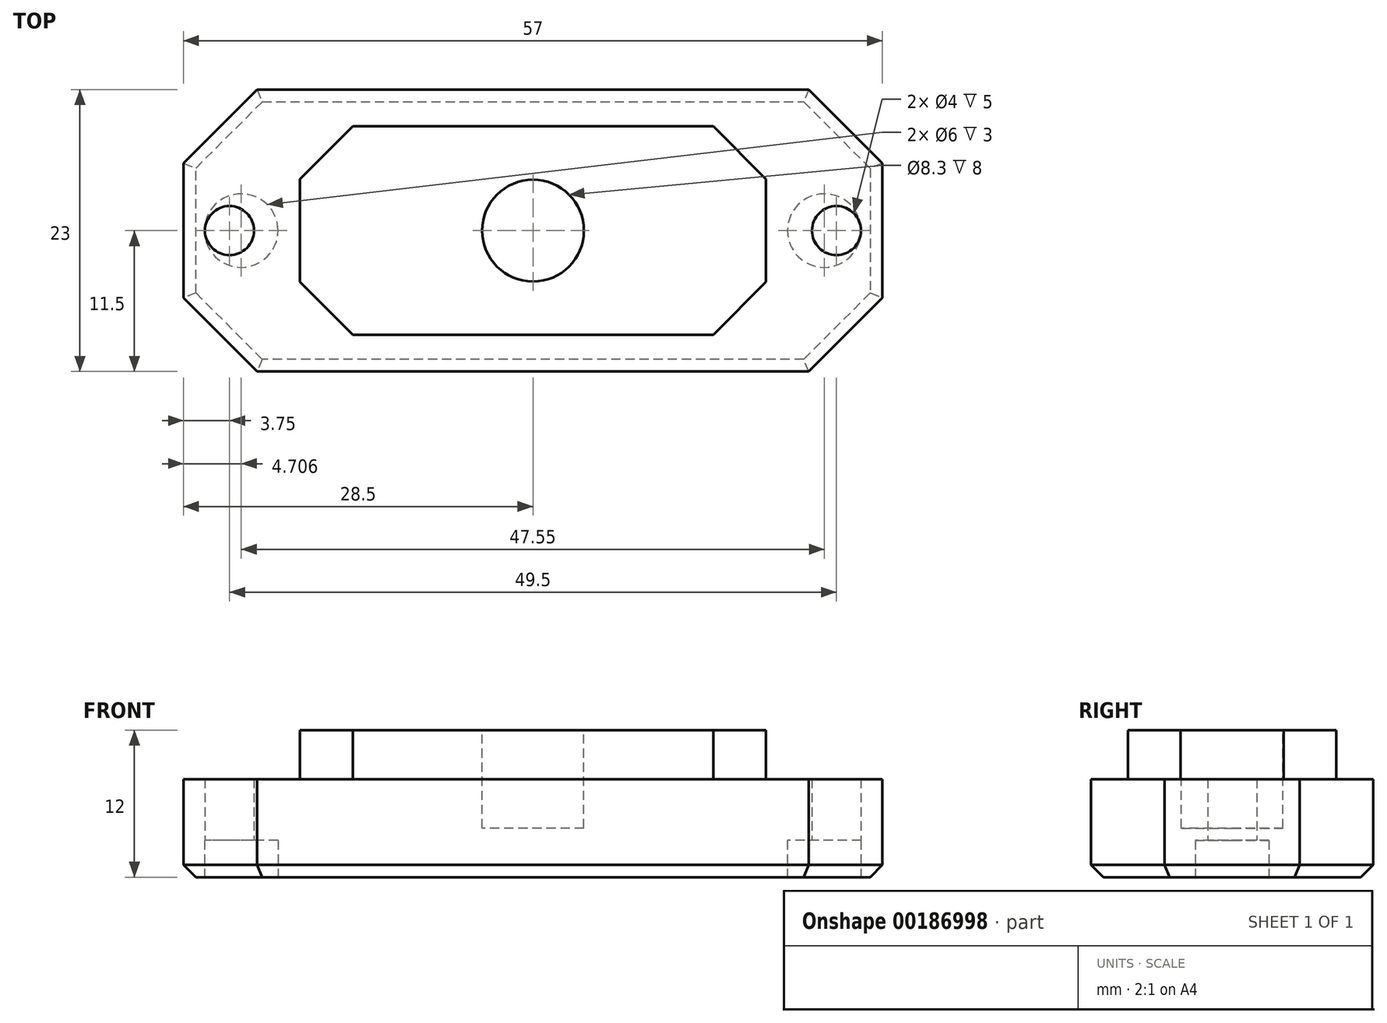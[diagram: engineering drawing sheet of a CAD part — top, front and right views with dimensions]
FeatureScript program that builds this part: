
annotation { "Feature Type Name" : "Feature", "Feature Type Description" : "" }
export const myFeature = defineFeature(function(context is Context, id is Id, definition is map)
    precondition{}
    {
        {
            var Q0;
            Q0=qCreatedBy(makeId("Top.planeOp"),FACE);
            var sketch = newSketch(context, id + "F0", { "sketchPlane" : qUnion([Q0])});
            skLineSegment(sketch, "E0.bottom", {"start": v(-14.7, 8.5) * mm, "end": v(14.7, 8.5) * mm});
            skLineSegment(sketch, "E0.top", {"start": v(-14.7, -8.5) * mm, "end": v(14.7, -8.5) * mm});
            skLineSegment(sketch, "E0.left", {"start": v(-19, 4.2) * mm, "end": v(-19, -4.2) * mm});
            skLineSegment(sketch, "E0.right", {"start": v(19, 4.2) * mm, "end": v(19, -4.2) * mm});
            skLineSegment(sketch, "E1.bottom", {"start": v(-22.5, 11.5) * mm, "end": v(22.5, 11.5) * mm});
            skLineSegment(sketch, "E1.top", {"start": v(-22.5, -11.5) * mm, "end": v(22.5, -11.5) * mm});
            skLineSegment(sketch, "E1.left", {"start": v(-28.5, 5.5) * mm, "end": v(-28.5, -5.5) * mm});
            skLineSegment(sketch, "E1.right", {"start": v(28.5, 5.5) * mm, "end": v(28.5, -5.5) * mm});
            skCircle(sketch, "E2", {"center": v(-24.75, 0) * mm, "radius": 2 * mm});
            skCircle(sketch, "E3.MirrorC", {"center": v(24.75, 0) * mm, "radius": 2 * mm});
            skLineSegment(sketch, "E4", {"start": v(-14.7, 8.5) * mm, "end": v(-19, 4.2) * mm});
            skLineSegment(sketch, "E5.MirrorCS", {"start": v(14.7, 8.5) * mm, "end": v(19, 4.2) * mm});
            skLineSegment(sketch, "E6.MirrorCS", {"start": v(-14.7, -8.5) * mm, "end": v(-19, -4.2) * mm});
            skLineSegment(sketch, "E7.MirrorCS", {"start": v(14.7, -8.5) * mm, "end": v(19, -4.2) * mm});
            skLineSegment(sketch, "E8", {"start": v(-28.5, 5.5) * mm, "end": v(-22.5, 11.5) * mm});
            skLineSegment(sketch, "E9.MirrorCS", {"start": v(28.5, 5.5) * mm, "end": v(22.5, 11.5) * mm});
            skLineSegment(sketch, "E10.MirrorCS", {"start": v(-28.5, -5.5) * mm, "end": v(-22.5, -11.5) * mm});
            skLineSegment(sketch, "E11.MirrorCS", {"start": v(28.5, -5.5) * mm, "end": v(22.5, -11.5) * mm});
            skPoint(sketch, "E12.orphan", {"position": v(-28.5, 11.5) * mm});
            skPoint(sketch, "E13.orphan", {"position": v(-19, 8.5) * mm});
            skSolve(sketch);
        }
        {
            var Q0;
            Q0=makeQuery(id+"F0.imprint","IMPRINT",FACE,{"disambiguationData":[TD([[makeQuery(id+"F0.imprint","IMPRINT",EDGE,{"derivedFrom":sQuery(id+"F0.wireOp",EDGE,"E0.bottom")}),-1.0]])]});
            extrude(context, id + "F1", {"entities" : qUnion([Q0]), "depth" : 12 * mm});
        }
        {
            var Q0;
            Q0=makeQuery(id+"F0.imprint","IMPRINT",FACE,{"disambiguationData":[TD([[makeQuery(id+"F0.imprint","IMPRINT",EDGE,{"derivedFrom":sQuery(id+"F0.wireOp",EDGE,"E0.bottom")}),1.0]])]});
            extrude(context, id + "F2", {"entities" : qUnion([Q0]), "operationType" : NewBodyOperationType.ADD, "depth" : 8 * mm});
        }
        {
            var Q0;
            Q0=makeQuery(id+"F2.opExtrude","CAP_EDGE",EDGE,{"disambiguationData":[OSD([sQuery(id+"F0.wireOp",EDGE,"E1.top")])],"isStart":true});
            var Q1;
            Q1=makeQuery(id+"F2.opExtrude","CAP_EDGE",EDGE,{"disambiguationData":[OSD([sQuery(id+"F0.wireOp",EDGE,"E10.MirrorCS")])],"isStart":true});
            var Q2;
            Q2=makeQuery(id+"F2.opExtrude","CAP_EDGE",EDGE,{"disambiguationData":[OSD([sQuery(id+"F0.wireOp",EDGE,"E1.left")])],"isStart":true});
            var Q3;
            Q3=makeQuery(id+"F2.opExtrude","CAP_EDGE",EDGE,{"disambiguationData":[OSD([sQuery(id+"F0.wireOp",EDGE,"E8")])],"isStart":true});
            var Q4;
            Q4=makeQuery(id+"F2.opExtrude","CAP_EDGE",EDGE,{"disambiguationData":[OSD([sQuery(id+"F0.wireOp",EDGE,"E1.bottom")])],"isStart":true});
            var Q5;
            Q5=makeQuery(id+"F2.opExtrude","CAP_EDGE",EDGE,{"disambiguationData":[OSD([sQuery(id+"F0.wireOp",EDGE,"E9.MirrorCS")])],"isStart":true});
            var Q6;
            Q6=makeQuery(id+"F2.opExtrude","CAP_EDGE",EDGE,{"disambiguationData":[OSD([sQuery(id+"F0.wireOp",EDGE,"E1.right")])],"isStart":true});
            var Q7;
            Q7=makeQuery(id+"F2.opExtrude","CAP_EDGE",EDGE,{"disambiguationData":[OSD([sQuery(id+"F0.wireOp",EDGE,"E11.MirrorCS")])],"isStart":true});
            chamfer(context, id + "F3", {"entities" : qUnion([Q0, Q1, Q2, Q3, Q4, Q5, Q6, Q7]), "width" : 1 * mm, "tangentPropagation" : true});
        }
        {
            var Q0;
            Q0=makeQuery(id+"F1.opExtrude","CAP_FACE",FACE,{"disambiguationData":[OSD([sQuery(id+"F0.wireOp",EDGE,"E0.bottom"),sQuery(id+"F0.wireOp",EDGE,"E0.top"),sQuery(id+"F0.wireOp",EDGE,"E0.left"),sQuery(id+"F0.wireOp",EDGE,"E0.right"),sQuery(id+"F0.wireOp",EDGE,"E4"),sQuery(id+"F0.wireOp",EDGE,"E5.MirrorCS"),sQuery(id+"F0.wireOp",EDGE,"E6.MirrorCS"),sQuery(id+"F0.wireOp",EDGE,"E7.MirrorCS")])],"isStart":false});
            var sketch = newSketch(context, id + "F4", { "sketchPlane" : qUnion([Q0])});
            skCircle(sketch, "E14", {"center": v(0, 0) * mm, "radius": 4.15 * mm});
            skSolve(sketch);
        }
        {
            var Q0;
            Q0=makeQuery(id+"F4.imprint","IMPRINT",FACE,{"disambiguationData":[TD([[makeQuery(id+"F4.imprint","IMPRINT",EDGE,{"derivedFrom":sQuery(id+"F4.wireOp",EDGE,"E14")}),1.0]])]});
            extrude(context, id + "F5", {"entities" : qUnion([Q0]), "operationType" : NewBodyOperationType.REMOVE, "oppositeDirection" : true, "depth" : 8 * mm});
        }
        {
            var Q0;
            Q0=qCreatedBy(makeId("Top.planeOp"),FACE);
            var sketch = newSketch(context, id + "F6", { "sketchPlane" : qUnion([Q0])});
            skCircle(sketch, "E15", {"center": v(-23.8, 0) * mm, "radius": 3 * mm});
            skCircle(sketch, "E16", {"center": v(23.76, 0) * mm, "radius": 3 * mm});
            skSolve(sketch);
        }
        {
            var Q0;
            Q0=qSketchRegion(id+"F6",true);
            extrude(context, id + "F7", {"entities" : qUnion([Q0]), "operationType" : NewBodyOperationType.REMOVE, "depth" : 3 * mm});
        }
    });
